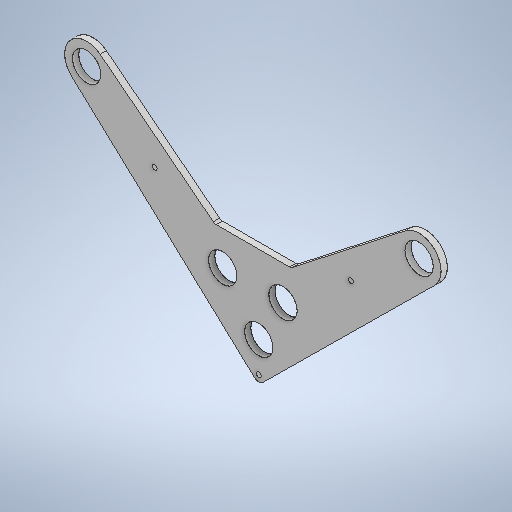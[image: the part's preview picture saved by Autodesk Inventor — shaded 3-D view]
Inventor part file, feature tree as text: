
AUTODESK INVENTOR PART (.ipt)
format: ipt  version: 2025.1 (Build 291241020, 241B)  size: 301,056 bytes
history: native  units: in
note: dims shown in document units (in); Inventor stores cm internally (conversion verified against a paired STEP export)
features: sketch x1, extrude x1
ambient origin geometry x8: Origin, YZ Plane, XZ Plane, XY Plane, X Axis, Y Axis, Z Axis, Center Point
bodies: Solid1 (feature_tree)
feature tree (2):
  sketch  "Sketch1"  dims[d0=4.0in d1=4.0in d2=0.196in d3=0.5in d4=3.4395in d5=0.5in d6=0.063in d7=0.196in d8=0.5in d9=0.196in d10=3.4395in d11=0.063in d12=0.188in d13=1.75in d14=1.75in d15=1.125in d16=0.7146in d17=6.879in d18=1.654in d19=1.504in d20=1.125in d21=0.063in d22=0.1in d23=2.4in d24=0.1in d25=1.6in d27=0.0in d28=0.25in]
  extrude  "Extrusion1"  [1 undecoded]
note: 1 required parameter value undecoded (feature->parameter linkage not recoverable at this tier; creation-order binding heuristic only, values carry confidence <= 0.55)
